# Revit family: 93801 102 CUBA DE SOBREPOR MORGANA MAXI 78X COM ACESSÓRIOS
name_source: partatom
category: Modelos genéricos
units: mm (PartAtom-declared; Revit-internal decimal feet)

## family parameters
Com base no plano de trabalho = Não
Compartilhado = Não
Corte com vazios quando carregada = Não
Cota do conector redondo = Utilizar diâmetro
Pode hospedar o vergalhão = Não
Ponto de cálculo do ambiente = Não
Sempre na vertical = Sim
Tipo de parte = Normal

## types (1)
- 93801 102 CUBA DE SOBREPOR MORGANA MAXI 78X COM ACESSÓRIOS
    Acabamento = Acetinado
    Acessórios inclusos = Kit de instalação, 1 Válvula 4 1/2, Tábua em madeira, Cesto coador e Dosador de sabão
    Capacidade = 56 L
    Descrição = Cuba de Sobrepor Morgana com Tábua Cesto e dosador
    Dimensões = 860 x 500 x 215 mm (Profundidade)
    Elevação padrão = 0 mm  [stored 0 ft]
    Espessura = 0,8 mm
    Fabricante = Tramontina
    Furo para torneira = Sim, 2 furos
    Manta adesiva Anti-ruído = Sim
    Material predominante = Aço Inox
    Modelo = Cuba de Sobrepor Morgana Maxi 78 FX com Tábua, cesto e dosador
    Nicho de instalação = Verificar folheto de instalação.
    Referência do produto = 93801/102
    Tipo de material = AISI 304
    URL da ficha técnica = https://assets.tramontina.com.br
    URL do fabricante = tramontina.com.br
    URL do produto = https://global.tramontina.com
    URL dos arquivos BIM = tramontina.com.br/biblioteca

note: [stored X ft] marks values corroborated as IEEE doubles in the binary element streams (Revit-internal decimal feet)
